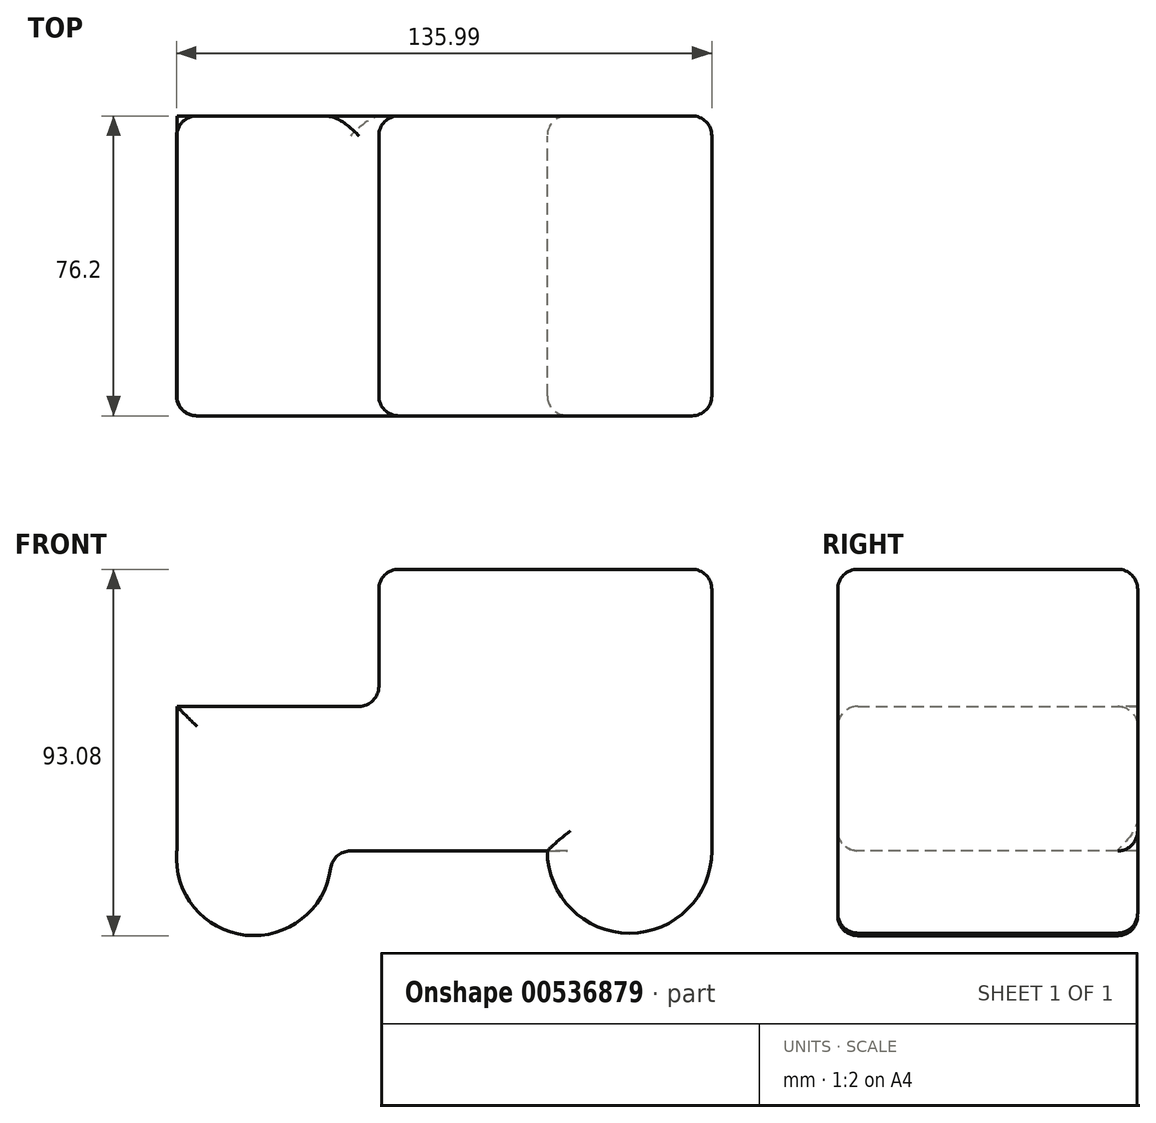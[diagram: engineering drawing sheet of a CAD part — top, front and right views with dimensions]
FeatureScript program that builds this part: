
annotation { "Feature Type Name" : "Feature", "Feature Type Description" : "" }
export const myFeature = defineFeature(function(context is Context, id is Id, definition is map)
    precondition{}
    {
        {
            var Q0;
            Q0=qCreatedBy(makeId("Front.planeOp"),FACE);
            var sketch = newSketch(context, id + "F0", { "sketchPlane" : qUnion([Q0])});
            skLineSegment(sketch, "E0", {"start": v(-60.31, 15.8) * mm, "end": v(-9, 15.8) * mm});
            skLineSegment(sketch, "E1", {"start": v(-9, 15.8) * mm, "end": v(-9, 50.64) * mm});
            skLineSegment(sketch, "E2", {"start": v(-9, 50.64) * mm, "end": v(75.6, 50.64) * mm});
            skLineSegment(sketch, "E3", {"start": v(-60.31, 15.8) * mm, "end": v(-60.31, -20.91) * mm});
            skLineSegment(sketch, "E4", {"start": v(-60.31, -20.91) * mm, "end": v(75.6, -20.91) * mm});
            skLineSegment(sketch, "E5", {"start": v(75.6, 50.64) * mm, "end": v(75.6, -20.91) * mm});
            skArc(sketch, "E6", {"start": v(-60.31, -20.91) * mm, "mid": v(-40.73, -42.44) * mm, "end": v(-21.16, -20.91) * mm});
            skArc(sketch, "E7", {"start": v(33.8, -20.91) * mm, "mid": v(54.7, -41.8) * mm, "end": v(75.6, -20.91) * mm});
            skLineSegment(sketch, "E8", {"start": v(-9, 15.8) * mm, "end": v(18.73, 15.8) * mm});
            skLineSegment(sketch, "E9", {"start": v(18.73, 15.8) * mm, "end": v(18.73, 50.64) * mm});
            skSolve(sketch);
        }
        {
            var Q0;
            Q0=makeQuery(id+"F0.imprint","IMPRINT",FACE,{"disambiguationData":[TD([[makeQuery(id+"F0.imprint","IMPRINT",EDGE,{"derivedFrom":sQuery(id+"F0.wireOp",EDGE,"E0")}),-1.0]])]});
            var Q1;
            {var subQ0=sQuery(id+"F0.wireOp",EDGE,"E1");Q1=makeQuery(id+"F0.imprint","IMPRINT",FACE,{"disambiguationData":[TD([[makeQuery(id+"F0.imprint","IMPRINT",EDGE,{"derivedFrom":subQ0}),-1.0]])]});}
            var Q2;
            {var subQ0=sQuery(id+"F0.wireOp",EDGE,"E6");Q2=makeQuery(id+"F0.imprint","IMPRINT",FACE,{"disambiguationData":[TD([[makeQuery(id+"F0.imprint","IMPRINT",EDGE,{"derivedFrom":subQ0}),1.0]])]});}
            var Q3;
            {var subQ0=sQuery(id+"F0.wireOp",EDGE,"E7");Q3=makeQuery(id+"F0.imprint","IMPRINT",FACE,{"disambiguationData":[TD([[makeQuery(id+"F0.imprint","IMPRINT",EDGE,{"derivedFrom":subQ0}),1.0]])]});}
            extrude(context, id + "F1", {"entities" : qUnion([Q0, Q1, Q2, Q3]), "depth" : 76.2 * mm, "offsetDistance" : 25.4 * mm});
        }
        {
            var Q0;
            Q0=makeQuery(id+"F1.opExtrude","CAP_EDGE",EDGE,{"disambiguationData":[OSD([sQuery(id+"F0.wireOp",EDGE,"E3")])],"isStart":false});
            var Q1;
            Q1=makeQuery(id+"F1.opExtrude","CAP_EDGE",EDGE,{"disambiguationData":[OSD([sQuery(id+"F0.wireOp",EDGE,"E0")])],"isStart":false});
            var Q2;
            Q2=makeQuery(id+"F1.opExtrude","CAP_EDGE",EDGE,{"disambiguationData":[OSD([sQuery(id+"F0.wireOp",EDGE,"E2")])],"isStart":false});
            var Q3;
            Q3=makeQuery(id+"F1.opExtrude","CAP_EDGE",EDGE,{"disambiguationData":[OSD([sQuery(id+"F0.wireOp",EDGE,"E1")])],"isStart":false});
            var Q4;
            Q4=makeQuery(id+"F1.opExtrude","CAP_EDGE",EDGE,{"disambiguationData":[OSD([sQuery(id+"F0.wireOp",EDGE,"E7")])],"isStart":false});
            var Q5;
            Q5=makeQuery(id+"F1.opExtrude","CAP_EDGE",EDGE,{"disambiguationData":[OSD([sQuery(id+"F0.wireOp",EDGE,"E6")])],"isStart":false});
            var Q6;
            Q6=makeQuery(id+"F1.opExtrude","CAP_EDGE",EDGE,{"disambiguationData":[OSD([sQuery(id+"F0.wireOp",EDGE,"E4")])],"isStart":false});
            var Q7;
            Q7=makeQuery(id+"F1.opExtrude","SWEPT_EDGE",EDGE,{"disambiguationData":[OSD([sQuery(id+"F0.wireOp",EDGE,"E2"),sQuery(id+"F0.wireOp",EDGE,"E5")])]});
            var Q8;
            Q8=makeQuery(id+"F1.opExtrude","CAP_EDGE",EDGE,{"disambiguationData":[OSD([sQuery(id+"F0.wireOp",EDGE,"E2")])],"isStart":true});
            var Q9;
            Q9=makeQuery(id+"F1.opExtrude","SWEPT_EDGE",EDGE,{"disambiguationData":[OSD([sQuery(id+"F0.wireOp",EDGE,"E1"),sQuery(id+"F0.wireOp",EDGE,"E2")])]});
            var Q10;
            Q10=makeQuery(id+"F1.opExtrude","SWEPT_FACE",FACE,{"disambiguationData":[OSD([sQuery(id+"F0.wireOp",EDGE,"E5")])]});
            var Q11;
            Q11=makeQuery(id+"F1.opExtrude","SWEPT_FACE",FACE,{"disambiguationData":[OSD([sQuery(id+"F0.wireOp",EDGE,"E1")])]});
            var Q12;
            Q12=makeQuery(id+"F1.opExtrude","SWEPT_EDGE",EDGE,{"disambiguationData":[OSD([sQuery(id+"F0.wireOp",EDGE,"E3"),sQuery(id+"F0.wireOp",EDGE,"E4"),sQuery(id+"F0.wireOp",EDGE,"E6")])]});
            var Q13;
            Q13=makeQuery(id+"F1.opExtrude","SWEPT_FACE",FACE,{"disambiguationData":[OSD([sQuery(id+"F0.wireOp",EDGE,"E6")])]});
            fillet(context, id + "F2", {"entities" : qUnion([Q0, Q1, Q2, Q3, Q4, Q5, Q6, Q7, Q8, Q9, Q10, Q11, Q12, Q13]), "radius" : 5.08 * mm, "tangentPropagation" : true, "allowEdgeOverflow" : false});
        }
    });
